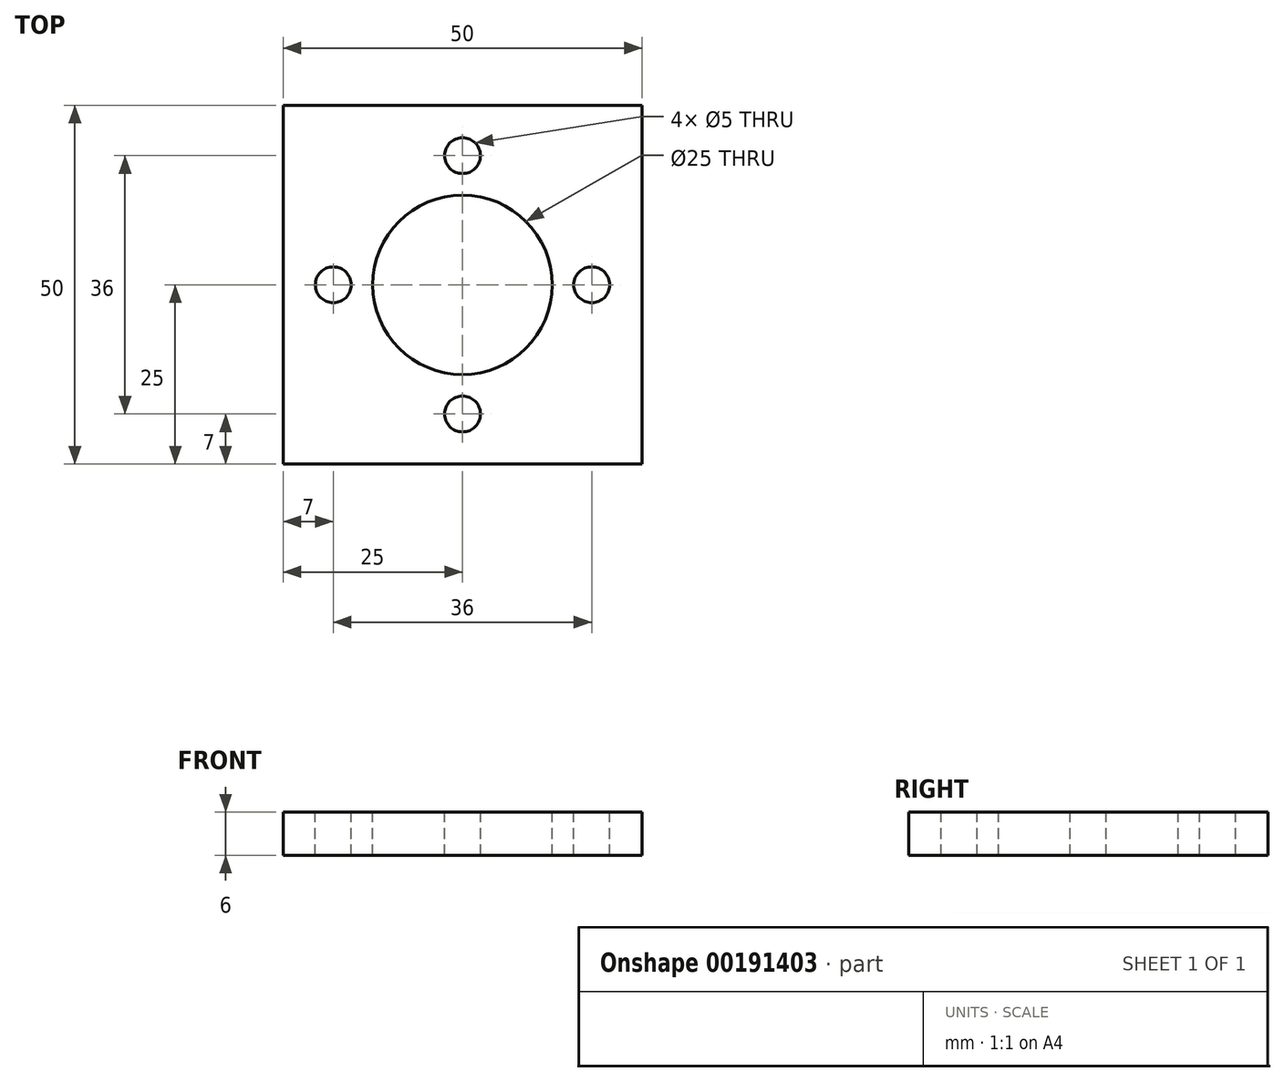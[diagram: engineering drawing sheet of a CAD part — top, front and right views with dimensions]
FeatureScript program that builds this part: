
annotation { "Feature Type Name" : "Feature", "Feature Type Description" : "" }
export const myFeature = defineFeature(function(context is Context, id is Id, definition is map)
    precondition{}
    {
        {
            var Q0;
            Q0=qCreatedBy(makeId("Top.planeOp"),FACE);
            var sketch = newSketch(context, id + "F0", { "sketchPlane" : qUnion([Q0])});
            skLineSegment(sketch, "E0.bottom", {"start": v(25, 25) * mm, "end": v(-25, 25) * mm});
            skLineSegment(sketch, "E0.top", {"start": v(25, -25) * mm, "end": v(-25, -25) * mm});
            skLineSegment(sketch, "E0.left", {"start": v(25, 25) * mm, "end": v(25, -25) * mm});
            skLineSegment(sketch, "E0.right", {"start": v(-25, 25) * mm, "end": v(-25, -25) * mm});
            skPoint(sketch, "E0.middle", {"position": v(0, 0) * mm});
            skSolve(sketch);
        }
        {
            var Q0;
            Q0=makeQuery(id+"F0.imprint","IMPRINT",FACE,{"disambiguationData":[TD([[makeQuery(id+"F0.imprint","IMPRINT",EDGE,{"derivedFrom":sQuery(id+"F0.wireOp",EDGE,"E0.bottom")}),1.0]])]});
            extrude(context, id + "F1", {"entities" : qUnion([Q0]), "depth" : 6 * mm});
        }
        {
            var Q0;
            Q0=makeQuery(id+"F1.opExtrude","CAP_FACE",FACE,{"disambiguationData":[OSD([sQuery(id+"F0.wireOp",EDGE,"E0.bottom"),sQuery(id+"F0.wireOp",EDGE,"E0.top"),sQuery(id+"F0.wireOp",EDGE,"E0.left"),sQuery(id+"F0.wireOp",EDGE,"E0.right")])],"isStart":false});
            var sketch = newSketch(context, id + "F2", { "sketchPlane" : qUnion([Q0])});
            skCircle(sketch, "E1", {"center": v(0, 0) * mm, "radius": 18 * mm});
            skPoint(sketch, "E2", {"position": v(0, 18) * mm});
            skPoint(sketch, "E3", {"position": v(18, 0) * mm});
            skPoint(sketch, "E4", {"position": v(0, -18) * mm});
            skPoint(sketch, "E5", {"position": v(-18, 0) * mm});
            skSolve(sketch);
        }
        {
            var Q0;
            Q0=sQuery(id+"F2.wireOp",VERTEX,"E2");
            var Q1;
            Q1=sQuery(id+"F2.wireOp",VERTEX,"E3");
            var Q2;
            Q2=sQuery(id+"F2.wireOp",VERTEX,"E4");
            var Q3;
            Q3=sQuery(id+"F2.wireOp",VERTEX,"E5");
            var Q4;
            Q4=makeQuery(id+"F1.opExtrude","SWEPT_BODY",BODY,{"disambiguationData":[OSD([sQuery(id+"F0.wireOp",EDGE,"E0.bottom"),sQuery(id+"F0.wireOp",EDGE,"E0.top"),sQuery(id+"F0.wireOp",EDGE,"E0.left"),sQuery(id+"F0.wireOp",EDGE,"E0.right")])]});
            hole(context, id + "F3", {"style" : HoleStyle.SIMPLE, "endStyle" : HoleEndStyle.THROUGH, "holeDiameter" : 5 * mm, "locations" : qUnion([Q0, Q1, Q2, Q3]), "scope" : qUnion([Q4]), "isTappedThrough" : true});
        }
        {
            var Q0;
            Q0=makeQuery(id+"F1.opExtrude","CAP_FACE",FACE,{"disambiguationData":[OSD([sQuery(id+"F0.wireOp",EDGE,"E0.bottom"),sQuery(id+"F0.wireOp",EDGE,"E0.top"),sQuery(id+"F0.wireOp",EDGE,"E0.left"),sQuery(id+"F0.wireOp",EDGE,"E0.right")])],"isStart":false});
            var sketch = newSketch(context, id + "F4", { "sketchPlane" : qUnion([Q0])});
            skPoint(sketch, "E6", {"position": v(0, 0) * mm});
            skSolve(sketch);
        }
        {
            var Q0;
            Q0=sQuery(id+"F4.wireOp",VERTEX,"E6");
            var Q1;
            Q1=makeQuery(id+"F1.opExtrude","SWEPT_BODY",BODY,{"disambiguationData":[OSD([sQuery(id+"F0.wireOp",EDGE,"E0.bottom"),sQuery(id+"F0.wireOp",EDGE,"E0.top"),sQuery(id+"F0.wireOp",EDGE,"E0.left"),sQuery(id+"F0.wireOp",EDGE,"E0.right")])]});
            hole(context, id + "F5", {"style" : HoleStyle.SIMPLE, "endStyle" : HoleEndStyle.THROUGH, "holeDiameter" : 25 * mm, "locations" : qUnion([Q0]), "scope" : qUnion([Q1]), "isTappedThrough" : true});
        }
    });
